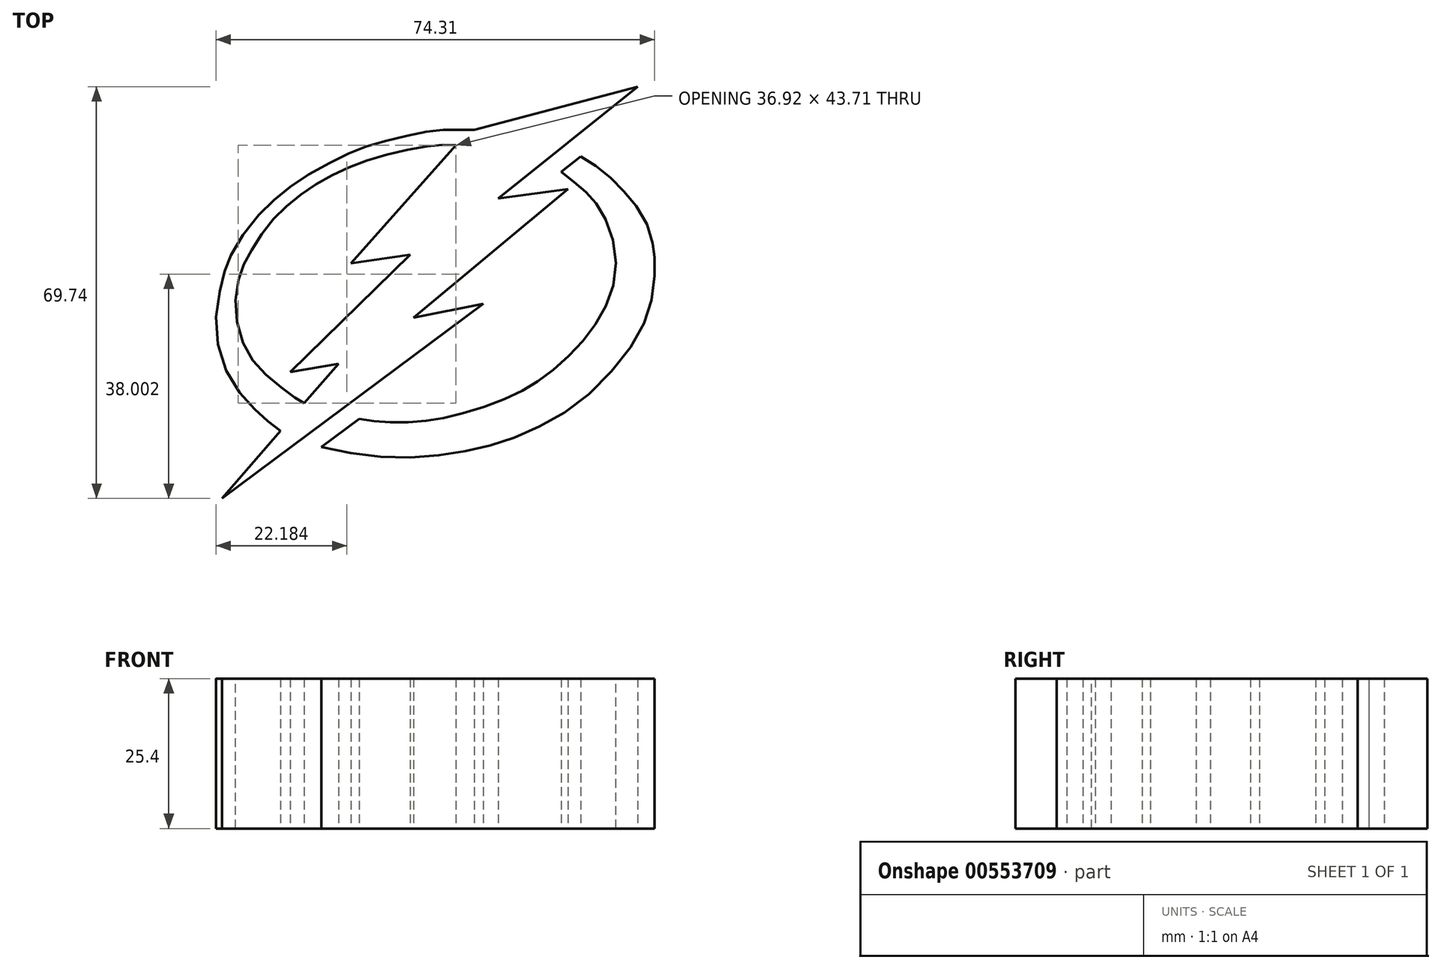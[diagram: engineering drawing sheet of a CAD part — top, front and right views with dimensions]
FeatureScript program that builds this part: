
annotation { "Feature Type Name" : "Feature", "Feature Type Description" : "" }
export const myFeature = defineFeature(function(context is Context, id is Id, definition is map)
    precondition{}
    {
        {
            var Q0;
            Q0=qCreatedBy(makeId("Top.planeOp"),FACE);
            var sketch = newSketch(context, id + "F0", { "sketchPlane" : qUnion([Q0])});
            skLineSegment(sketch, "E0", {"start": v(0.97, 0.14) * mm, "end": v(45.22, 33.12) * mm});
            skLineSegment(sketch, "E1", {"start": v(45.22, 33.12) * mm, "end": v(33.38, 30.74) * mm});
            skLineSegment(sketch, "E2", {"start": v(33.38, 30.74) * mm, "end": v(59.57, 52.52) * mm});
            skLineSegment(sketch, "E3", {"start": v(59.57, 52.52) * mm, "end": v(47.77, 50.99) * mm});
            skLineSegment(sketch, "E4", {"start": v(47.77, 50.99) * mm, "end": v(71.4, 69.88) * mm});
            skLineSegment(sketch, "E5", {"start": v(71.4, 69.88) * mm, "end": v(43.69, 62.58) * mm});
            skLineSegment(sketch, "E6", {"start": v(40.58, 60) * mm, "end": v(22.8, 39.95) * mm});
            skLineSegment(sketch, "E7", {"start": v(22.8, 39.95) * mm, "end": v(32.84, 41.44) * mm});
            skLineSegment(sketch, "E8", {"start": v(32.84, 41.44) * mm, "end": v(12.52, 21.58) * mm});
            skLineSegment(sketch, "E9", {"start": v(10.86, 11.58) * mm, "end": v(0.97, 0.14) * mm});
            skFitSpline(sketch, "E10", {"points": [v(40.58, 60) * mm, v(37.79, 60) * mm, v(33, 59.3) * mm, v(26.15, 57.6) * mm, v(21, 55.56) * mm, v(16.28, 52.98) * mm, v(12.1, 49.78) * mm, v(8.47, 46.05) * mm, v(5.53, 41.43) * mm, v(3.93, 37.97) * mm, v(3.31, 31.48) * mm, v(5.36, 24.73) * mm, v(9.27, 20.37) * mm, v(13.26, 17.26) * mm, v(14.86, 16.29) * mm], "startDerivative": vector(-49.54, 1.86) * mm, "endDerivative": vector(32.66, -18.47) * mm});
            skLineSegment(sketch, "E11", {"start": v(14.86, 16.29) * mm, "end": v(20.7, 22.96) * mm});
            skLineSegment(sketch, "E12", {"start": v(20.7, 22.96) * mm, "end": v(12.52, 21.58) * mm});
            skLineSegment(sketch, "E13", {"start": v(61.7, 58.08) * mm, "end": v(58.42, 55.48) * mm});
            skFitSpline(sketch, "E14", {"points": [v(24.22, 13.64) * mm, v(28.57, 13.08) * mm, v(34.46, 13.2) * mm, v(40.48, 14.24) * mm, v(49.03, 17.07) * mm, v(54.81, 20.25) * mm, v(60.6, 25.16) * mm, v(65.4, 31.58) * mm, v(67.7, 40.31) * mm, v(65.16, 48.92) * mm, v(62.16, 52.45) * mm, v(58.42, 55.48) * mm], "startDerivative": vector(56.39, -9.35) * mm, "endDerivative": vector(-50.59, 39.45) * mm});
            skFitSpline(sketch, "E15", {"points": [v(61.7, 58.08) * mm, v(64.37, 56.42) * mm, v(67.07, 54.16) * mm, v(69.44, 51.7) * mm, v(71.74, 48.78) * mm, v(73.64, 44.8) * mm, v(74.1, 41.97) * mm, v(74.24, 40.35) * mm, v(74.03, 35.75) * mm, v(72.58, 30.1) * mm, v(68.57, 23.64) * mm, v(61.7, 16.64) * mm, v(54.63, 12.3) * mm, v(48.11, 9.62) * mm, v(42.1, 8.13) * mm, v(34.91, 7.19) * mm, v(26.35, 7.36) * mm, v(17.77, 8.83) * mm], "startDerivative": vector(59.82, -34.47) * mm, "endDerivative": vector(-114.23, 23.29) * mm});
            skFitSpline(sketch, "E16", {"points": [v(43.69, 62.58) * mm, v(41.7, 62.58) * mm, v(38.03, 62.58) * mm, v(34.46, 62.07) * mm, v(29, 60.8) * mm, v(24.49, 59.44) * mm, v(20.55, 57.66) * mm, v(14.72, 54.47) * mm, v(10.47, 51.3) * mm, v(6.42, 47.32) * mm, v(2.49, 41.43) * mm, v(1.23, 37.97) * mm, v(0, 31.48) * mm, v(1.22, 22.73) * mm, v(5.36, 16.43) * mm, v(8.47, 13.43) * mm, v(10.86, 11.58) * mm], "startDerivative": vector(-45.87, -0.46) * mm, "endDerivative": vector(48.73, -36.24) * mm});
            skLineSegment(sketch, "E17", {"start": v(24.22, 13.64) * mm, "end": v(17.77, 8.83) * mm});
            skSolve(sketch);
        }
        {
            var Q0;
            Q0 = qSketchRegion(id + "F0", true);
            extrude(context, id + "F1", {"entities" : qUnion([Q0]), "depth" : 25.4 * mm, "offsetDistance" : 25.4 * mm});
        }
    });
